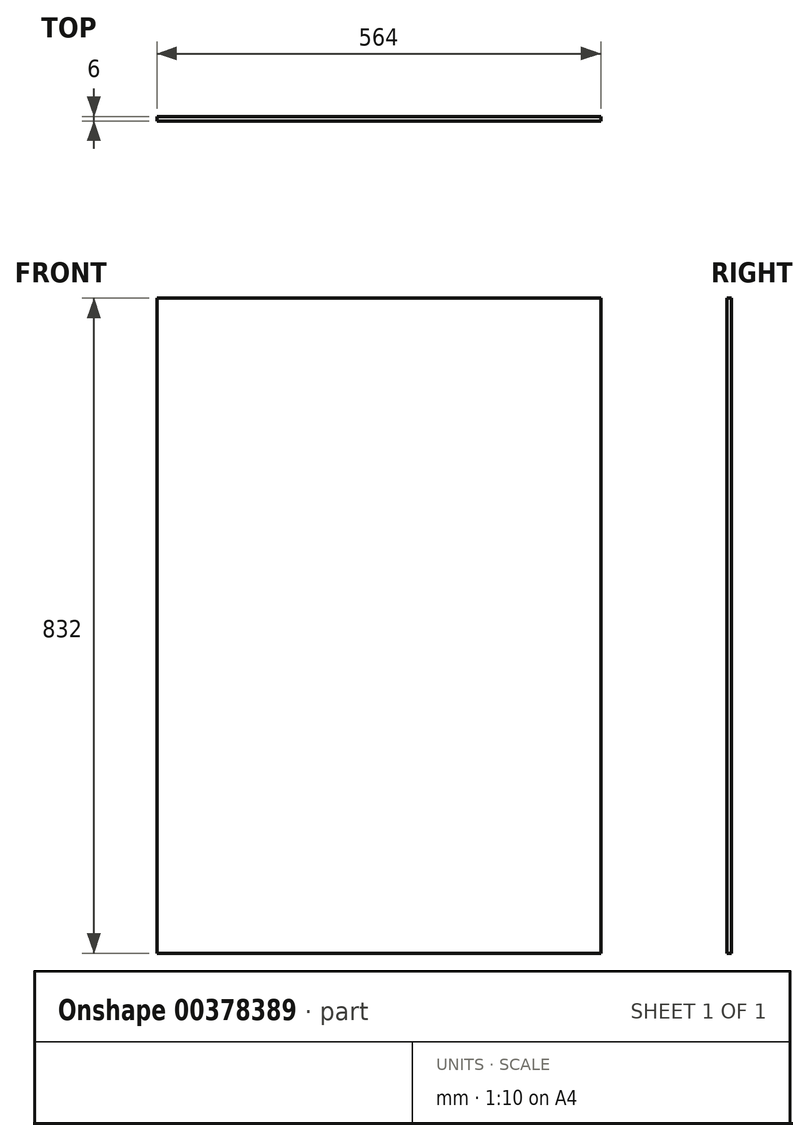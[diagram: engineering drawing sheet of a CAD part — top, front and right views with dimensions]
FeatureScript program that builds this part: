
annotation { "Feature Type Name" : "Feature", "Feature Type Description" : "" }
export const myFeature = defineFeature(function(context is Context, id is Id, definition is map)
    precondition{}
    {
        {
            var Q0;
            Q0=qCreatedBy(makeId("Front.planeOp"),FACE);
            var sketch = newSketch(context, id + "F0", { "sketchPlane" : qUnion([Q0])});
            skLineSegment(sketch, "E0.bottom", {"start": v(282, 416) * mm, "end": v(-282, 416) * mm});
            skLineSegment(sketch, "E0.top", {"start": v(282, -416) * mm, "end": v(-282, -416) * mm});
            skLineSegment(sketch, "E0.left", {"start": v(282, 416) * mm, "end": v(282, -416) * mm});
            skLineSegment(sketch, "E0.right", {"start": v(-282, 416) * mm, "end": v(-282, -416) * mm});
            skPoint(sketch, "E0.middle", {"position": v(0, 0) * mm});
            skSolve(sketch);
        }
        {
            var Q0;
            Q0 = qSketchRegion(id + "F0", true);
            extrude(context, id + "F1", {"entities" : qUnion([Q0]), "depth" : 6 * mm});
        }
    });
